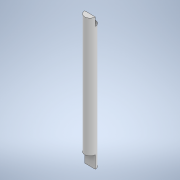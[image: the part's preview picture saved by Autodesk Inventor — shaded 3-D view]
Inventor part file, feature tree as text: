
AUTODESK INVENTOR PART (.ipt)
format: ipt  version: 2022 (Build 260153000, 153)  size: 104,960 bytes
history: native  units: mm
features: extrude x3, sketch x3
ambient origin geometry x8: Origin, YZ Plane, XZ Plane, XY Plane, X Axis, Y Axis, Z Axis, Center Point
bodies: Solid1 (feature_tree)
feature tree (6):
  extrude  "Extrusion1"  Depth=65.0mm TaperAngle=0.0deg
  extrude  "Extrusion2"  Depth=6.2mm TaperAngle=0.0deg
  extrude  "Extrusion3"  [1 undecoded]
  sketch  "Sketch1"  dims[d0=5.25mm d1=65.0mm d2=0.0mm]
  sketch  "Sketch2"  dims[d3=4.0mm d4=0.0mm d5=6.2mm d6=0.0mm]
  sketch  "Sketch3"
note: 1 required parameter value undecoded (feature->parameter linkage not recoverable at this tier; creation-order binding heuristic only, values carry confidence <= 0.55)
